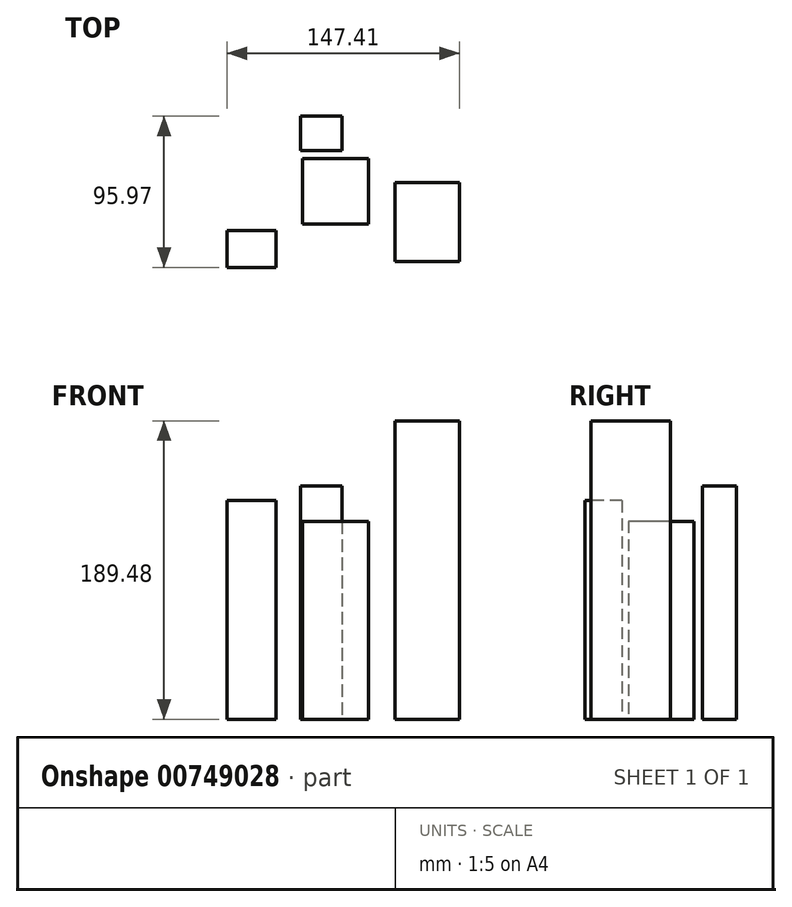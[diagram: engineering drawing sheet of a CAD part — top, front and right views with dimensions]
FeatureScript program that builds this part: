
annotation { "Feature Type Name" : "Feature", "Feature Type Description" : "" }
export const myFeature = defineFeature(function(context is Context, id is Id, definition is map)
    precondition{}
    {
        {
            var Q0;
            Q0=qCreatedBy(makeId("Top.planeOp"),FACE);
            var sketch = newSketch(context, id + "F0", { "sketchPlane" : qUnion([Q0])});
            skLineSegment(sketch, "E0.bottom", {"start": v(0, 0) * mm, "end": v(-41.98, 0) * mm});
            skLineSegment(sketch, "E0.top", {"start": v(0, -41.53) * mm, "end": v(-41.98, -41.53) * mm});
            skLineSegment(sketch, "E0.left", {"start": v(0, 0) * mm, "end": v(0, -41.53) * mm});
            skLineSegment(sketch, "E0.right", {"start": v(-41.98, 0) * mm, "end": v(-41.98, -41.53) * mm});
            skSolve(sketch);
        }
        {
            var Q0;
            Q0 = qSketchRegion(id + "F0", true);
            extrude(context, id + "F1", {"entities" : qUnion([Q0]), "depth" : 125.73 * mm, "offsetDistance" : 25.4 * mm});
        }
        {
            var Q0;
            Q0=qCreatedBy(makeId("Top.planeOp"),FACE);
            var sketch = newSketch(context, id + "F2", { "sketchPlane" : qUnion([Q0])});
            skLineSegment(sketch, "E1.bottom", {"start": v(16.7, -15.12) * mm, "end": v(57.61, -15.12) * mm});
            skLineSegment(sketch, "E1.top", {"start": v(16.7, -65.42) * mm, "end": v(57.61, -65.42) * mm});
            skLineSegment(sketch, "E1.left", {"start": v(16.7, -15.12) * mm, "end": v(16.7, -65.42) * mm});
            skLineSegment(sketch, "E1.right", {"start": v(57.61, -15.12) * mm, "end": v(57.61, -65.42) * mm});
            skSolve(sketch);
        }
        {
            var Q0;
            Q0 = qSketchRegion(id + "F2", true);
            extrude(context, id + "F3", {"entities" : qUnion([Q0]), "depth" : 189.48 * mm, "offsetDistance" : 25.4 * mm});
        }
        {
            var Q0;
            Q0=qCreatedBy(makeId("Top.planeOp"),FACE);
            var sketch = newSketch(context, id + "F4", { "sketchPlane" : qUnion([Q0])});
            skLineSegment(sketch, "E2.bottom", {"start": v(-58.83, -45.83) * mm, "end": v(-89.8, -45.83) * mm});
            skLineSegment(sketch, "E2.top", {"start": v(-58.83, -69.14) * mm, "end": v(-89.8, -69.14) * mm});
            skLineSegment(sketch, "E2.left", {"start": v(-58.83, -45.83) * mm, "end": v(-58.83, -69.14) * mm});
            skLineSegment(sketch, "E2.right", {"start": v(-89.8, -45.83) * mm, "end": v(-89.8, -69.14) * mm});
            skSolve(sketch);
        }
        {
            var Q0;
            Q0 = qSketchRegion(id + "F4", true);
            extrude(context, id + "F5", {"entities" : qUnion([Q0]), "depth" : 138.94 * mm, "offsetDistance" : 25.4 * mm});
        }
        {
            var Q0;
            Q0=qCreatedBy(makeId("Top.planeOp"),FACE);
            var sketch = newSketch(context, id + "F6", { "sketchPlane" : qUnion([Q0])});
            skLineSegment(sketch, "E3.bottom", {"start": v(-43.1, 26.83) * mm, "end": v(-16.75, 26.83) * mm});
            skLineSegment(sketch, "E3.top", {"start": v(-43.1, 5.21) * mm, "end": v(-16.75, 5.21) * mm});
            skLineSegment(sketch, "E3.left", {"start": v(-43.1, 26.83) * mm, "end": v(-43.1, 5.21) * mm});
            skLineSegment(sketch, "E3.right", {"start": v(-16.75, 26.83) * mm, "end": v(-16.75, 5.21) * mm});
            skSolve(sketch);
        }
        {
            var Q0;
            Q0=makeQuery(id+"F6.imprint","IMPRINT",FACE,{"disambiguationData":[TD([[makeQuery(id+"F6.imprint","IMPRINT",EDGE,{"derivedFrom":sQuery(id+"F6.wireOp",EDGE,"E3.bottom")}),-1.0]])]});
            extrude(context, id + "F7", {"entities" : qUnion([Q0]), "depth" : 148.08 * mm, "offsetDistance" : 25.4 * mm});
        }
    });
